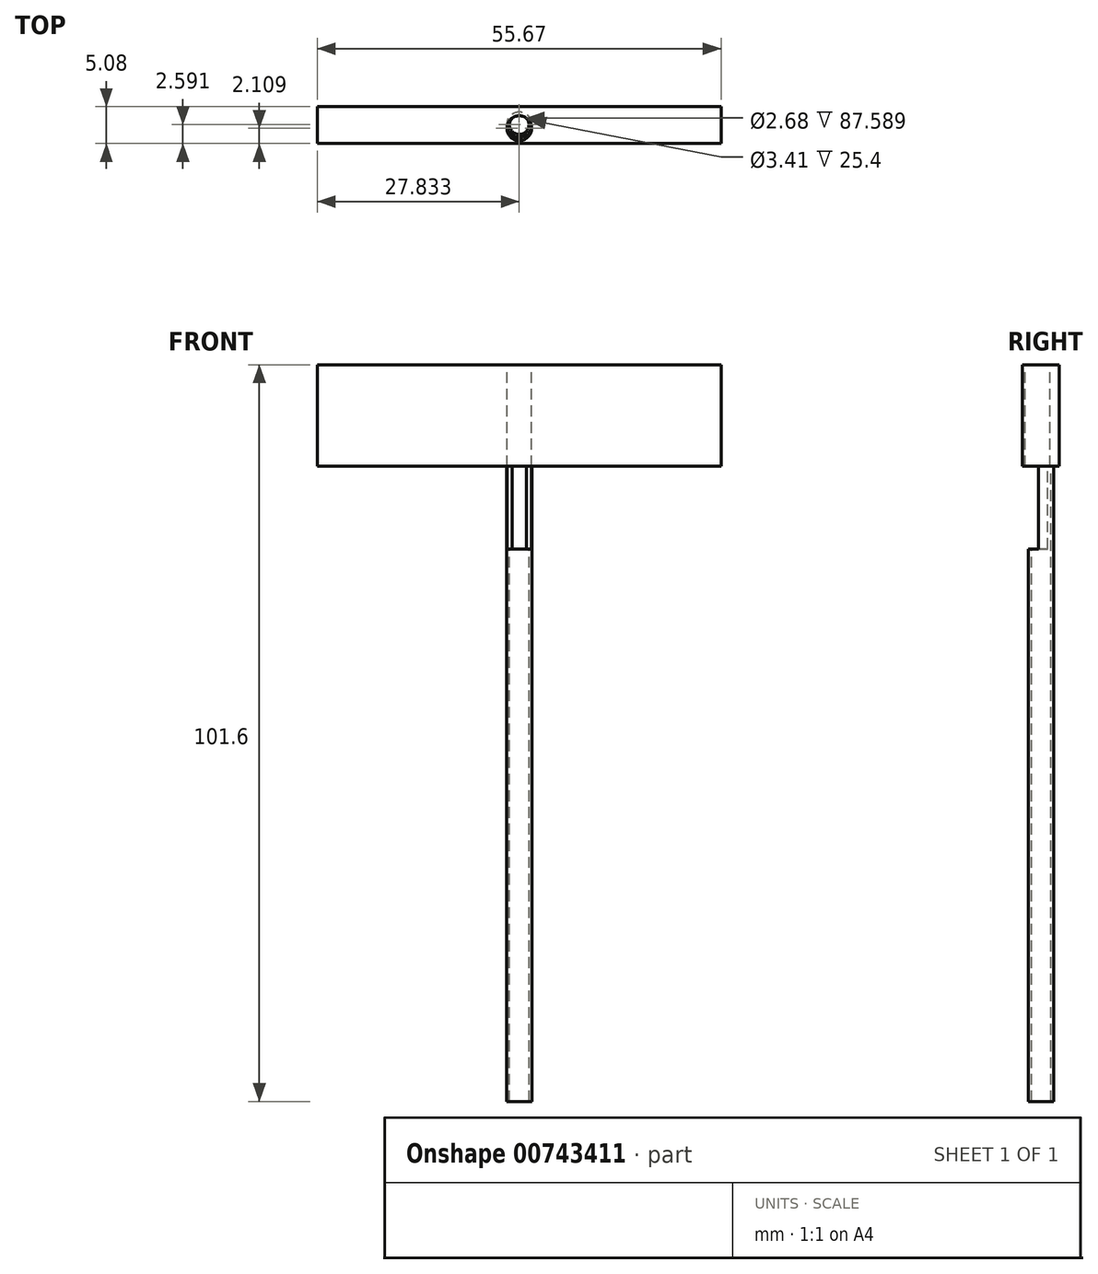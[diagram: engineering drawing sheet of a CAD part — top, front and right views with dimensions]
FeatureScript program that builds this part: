
annotation { "Feature Type Name" : "Feature", "Feature Type Description" : "" }
export const myFeature = defineFeature(function(context is Context, id is Id, definition is map)
    precondition{}
    {
        {
            var Q0;
            Q0=qCreatedBy(makeId("Front.planeOp"),FACE);
            var sketch = newSketch(context, id + "F0", { "sketchPlane" : qUnion([Q0])});
            skLineSegment(sketch, "E0.bottom", {"start": v(-13.73, 19.08) * mm, "end": v(41.94, 19.08) * mm});
            skLineSegment(sketch, "E0.top", {"start": v(-13.73, 5.07) * mm, "end": v(41.94, 5.07) * mm});
            skLineSegment(sketch, "E0.left", {"start": v(-13.73, 19.08) * mm, "end": v(-13.73, 5.07) * mm});
            skLineSegment(sketch, "E0.right", {"start": v(41.94, 19.08) * mm, "end": v(41.94, 5.07) * mm});
            skSolve(sketch);
        }
        {
            var Q0;
            Q0=makeQuery(id+"F0.imprint","IMPRINT",FACE,{"disambiguationData":[TD([[makeQuery(id+"F0.imprint","IMPRINT",EDGE,{"derivedFrom":sQuery(id+"F0.wireOp",EDGE,"E0.bottom")}),-1.0]])]});
            extrude(context, id + "F1", {"entities" : qUnion([Q0]), "depth" : 5.08 * mm, "offsetDistance" : 25.4 * mm});
        }
        {
            var Q0;
            Q0=makeQuery(id+"F1.opExtrude","SWEPT_FACE",FACE,{"disambiguationData":[OSD([sQuery(id+"F0.wireOp",EDGE,"E0.bottom")])]});
            var sketch = newSketch(context, id + "F2", { "sketchPlane" : qUnion([Q0])});
            skCircle(sketch, "E1", {"center": v(14.1, -2.49) * mm, "radius": 1.34 * mm});
            skPoint(sketch, "E1.centerSnap0", {"position": v(14.1, -5.08) * mm});
            skCircle(sketch, "E2", {"center": v(14.1, -2.49) * mm, "radius": 1.74 * mm});
            skSolve(sketch);
        }
        {
            var Q0;
            Q0 = qSketchRegion(id + "F2", true);
            extrude(context, id + "F3", {"entities" : qUnion([Q0]), "operationType" : NewBodyOperationType.ADD, "oppositeDirection" : true, "depth" : 101.6 * mm, "offsetDistance" : 25.4 * mm});
        }
        {
            var Q0;
            Q0=makeQuery(id+"F1.opExtrude","SWEPT_FACE",FACE,{"disambiguationData":[OSD([sQuery(id+"F0.wireOp",EDGE,"E0.bottom")])]});
            var sketch = newSketch(context, id + "F4", { "sketchPlane" : qUnion([Q0])});
            skCircle(sketch, "E3", {"center": v(14.1, -2.97) * mm, "radius": 1.7 * mm});
            skPoint(sketch, "E3.centerSnap0", {"position": v(14.1, -5.08) * mm});
            skSolve(sketch);
        }
        {
            var Q0;
            Q0=makeQuery(id+"F4.imprint","IMPRINT",FACE,{"disambiguationData":[TD([[makeQuery(id+"F4.imprint","IMPRINT",EDGE,{"derivedFrom":sQuery(id+"F4.wireOp",EDGE,"E3")}),1.0]])]});
            extrude(context, id + "F5", {"entities" : qUnion([Q0]), "operationType" : NewBodyOperationType.REMOVE, "oppositeDirection" : true, "depth" : 25.4 * mm, "offsetDistance" : 25.4 * mm});
        }
    });
